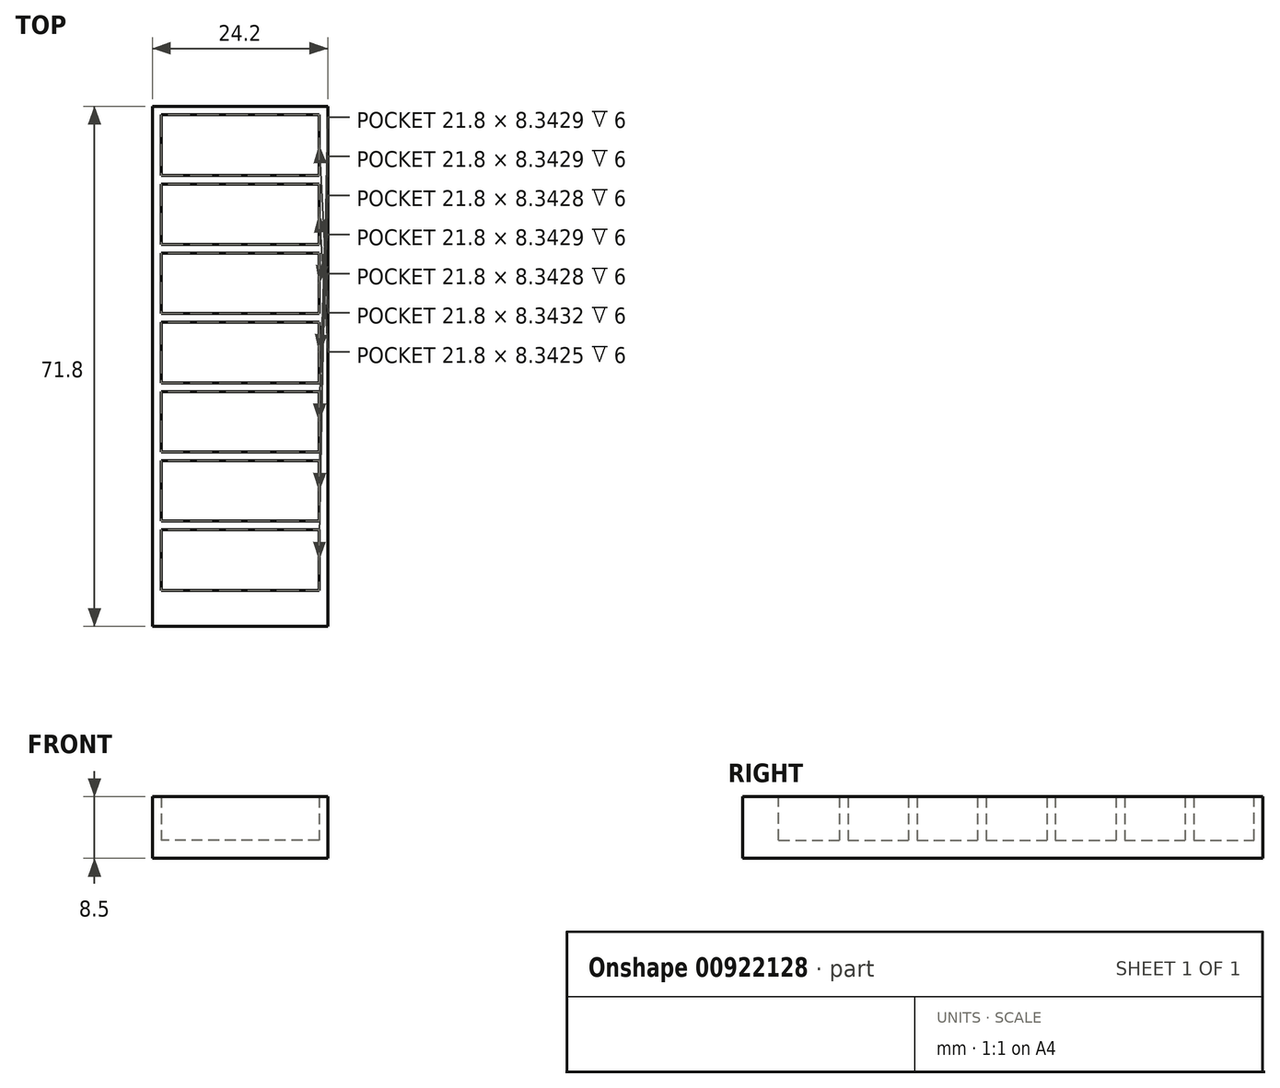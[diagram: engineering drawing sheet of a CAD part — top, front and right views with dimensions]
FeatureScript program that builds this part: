
annotation { "Feature Type Name" : "Feature", "Feature Type Description" : "" }
export const myFeature = defineFeature(function(context is Context, id is Id, definition is map)
    precondition{}
    {
        {
            var Q0;
            Q0=qCreatedBy(makeId("Top.planeOp"),FACE);
            var sketch = newSketch(context, id + "F0", { "sketchPlane" : qUnion([Q0])});
            skLineSegment(sketch, "E0.bottom", {"start": v(0, 0) * mm, "end": v(24.2, 0) * mm});
            skLineSegment(sketch, "E0.top", {"start": v(0, 71.8) * mm, "end": v(24.2, 71.8) * mm});
            skLineSegment(sketch, "E0.left", {"start": v(0, 0) * mm, "end": v(0, 71.8) * mm});
            skLineSegment(sketch, "E0.right", {"start": v(24.2, 0) * mm, "end": v(24.2, 71.8) * mm});
            skSolve(sketch);
        }
        {
            var Q0;
            Q0=qSketchRegion(id+"F0",true);
            extrude(context, id + "F1", {"entities" : qUnion([Q0]), "depth" : 8.5 * mm, "offsetDistance" : 25 * mm});
        }
        {
            var Q0;
            Q0=makeQuery(id+"F1.opExtrude","CAP_FACE",FACE,{"disambiguationData":[OSD([sQuery(id+"F0.wireOp",EDGE,"E0.bottom"),sQuery(id+"F0.wireOp",EDGE,"E0.top"),sQuery(id+"F0.wireOp",EDGE,"E0.left"),sQuery(id+"F0.wireOp",EDGE,"E0.right")])],"isStart":false});
            var sketch = newSketch(context, id + "F2", { "sketchPlane" : qUnion([Q0])});
            skLineSegment(sketch, "E1.0", {"start": v(1.2, 70.6) * mm, "end": v(23, 70.6) * mm});
            skLineSegment(sketch, "E2.0", {"start": v(23, 5) * mm, "end": v(23, 70.6) * mm});
            skLineSegment(sketch, "E3.0", {"start": v(1.2, 5) * mm, "end": v(1.2, 70.6) * mm});
            skLineSegment(sketch, "E4.0", {"start": v(1.2, 5) * mm, "end": v(23, 5) * mm});
            skSolve(sketch);
        }
        {
            var Q0;
            Q0=qSketchRegion(id+"F2",true);
            extrude(context, id + "F3", {"entities" : qUnion([Q0]), "operationType" : NewBodyOperationType.REMOVE, "oppositeDirection" : true, "depth" : 6 * mm, "offsetDistance" : 25 * mm});
        }
        {
            var Q0;
            Q0=makeQuery(id+"F3.boolean.opBoolean","COPY",FACE,{"derivedFrom":makeQuery(id+"F3.opExtrude","CAP_FACE",FACE,{"disambiguationData":[OSD([sQuery(id+"F2.wireOp",EDGE,"E1.0"),sQuery(id+"F2.wireOp",EDGE,"E2.0"),sQuery(id+"F2.wireOp",EDGE,"E3.0"),sQuery(id+"F2.wireOp",EDGE,"E4.0")])],"isStart":false})});
            var sketch = newSketch(context, id + "F4", { "sketchPlane" : qUnion([Q0])});
            skLineSegment(sketch, "E5.bottom", {"start": v(12, 70.6) * mm, "end": v(13.2, 70.6) * mm});
            skLineSegment(sketch, "E5.top", {"start": v(12, 5) * mm, "end": v(13.2, 5) * mm});
            skLineSegment(sketch, "E6.bottom", {"start": v(11, 70.6) * mm, "end": v(12.2, 70.6) * mm});
            skLineSegment(sketch, "E6.top", {"start": v(11, 5) * mm, "end": v(12.2, 5) * mm});
            skLineSegment(sketch, "E7", {"start": v(23, 70.6) * mm, "end": v(23, 5) * mm, "construction": true});
            skLineSegment(sketch, "E8", {"start": v(23, 5) * mm, "end": v(1.2, 5) * mm, "construction": true});
            skLineSegment(sketch, "E9.bottom", {"start": v(1.2, 62.26) * mm, "end": v(12.18, 62.26) * mm});
            skLineSegment(sketch, "E9.top", {"start": v(1.2, 61.06) * mm, "end": v(12, 61.06) * mm});
            skLineSegment(sketch, "E9.left", {"start": v(1.2, 62.26) * mm, "end": v(1.2, 61.06) * mm});
            skLineSegment(sketch, "E9.right", {"start": v(23, 62.26) * mm, "end": v(23, 61.06) * mm});
            skLineSegment(sketch, "E10.bottom", {"start": v(23, 52.71) * mm, "end": v(12.2, 52.71) * mm});
            skLineSegment(sketch, "E10.top", {"start": v(23, 51.51) * mm, "end": v(12.2, 51.51) * mm});
            skLineSegment(sketch, "E10.left", {"start": v(23, 52.71) * mm, "end": v(23, 51.51) * mm});
            skLineSegment(sketch, "E10.right", {"start": v(1.2, 52.71) * mm, "end": v(1.2, 51.51) * mm});
            skLineSegment(sketch, "E11.bottom", {"start": v(1.2, 43.17) * mm, "end": v(12, 43.17) * mm});
            skLineSegment(sketch, "E11.top", {"start": v(1.2, 41.97) * mm, "end": v(12, 41.97) * mm});
            skLineSegment(sketch, "E11.left", {"start": v(1.2, 43.17) * mm, "end": v(1.2, 41.97) * mm});
            skLineSegment(sketch, "E11.right", {"start": v(23, 43.17) * mm, "end": v(23, 41.97) * mm});
            skLineSegment(sketch, "E12.bottom", {"start": v(23, 33.63) * mm, "end": v(12.2, 33.63) * mm});
            skLineSegment(sketch, "E12.top", {"start": v(23, 32.43) * mm, "end": v(12.2, 32.43) * mm});
            skLineSegment(sketch, "E12.left", {"start": v(23, 33.63) * mm, "end": v(23, 32.43) * mm});
            skLineSegment(sketch, "E12.right", {"start": v(1.2, 33.63) * mm, "end": v(1.2, 32.43) * mm});
            skLineSegment(sketch, "E13.bottom", {"start": v(1.2, 24.09) * mm, "end": v(12, 24.09) * mm});
            skLineSegment(sketch, "E13.top", {"start": v(1.2, 22.89) * mm, "end": v(12, 22.89) * mm});
            skLineSegment(sketch, "E13.left", {"start": v(1.2, 24.09) * mm, "end": v(1.2, 22.89) * mm});
            skLineSegment(sketch, "E13.right", {"start": v(23, 24.09) * mm, "end": v(23, 22.89) * mm});
            skLineSegment(sketch, "E14.bottom", {"start": v(23, 14.54) * mm, "end": v(12.2, 14.54) * mm});
            skLineSegment(sketch, "E14.top", {"start": v(23, 13.34) * mm, "end": v(12.2, 13.34) * mm});
            skLineSegment(sketch, "E14.left", {"start": v(23, 14.54) * mm, "end": v(23, 13.34) * mm});
            skLineSegment(sketch, "E14.right", {"start": v(1.2, 14.54) * mm, "end": v(1.2, 13.34) * mm});
            skLineSegment(sketch, "E15.trimOffspring", {"start": v(1, 62.26) * mm, "end": v(11, 62.26) * mm});
            skLineSegment(sketch, "E16.trimOffspring", {"start": v(11, 61.06) * mm, "end": v(13.2, 61.06) * mm});
            skLineSegment(sketch, "E17.trimOffspring", {"start": v(12.02, 62.26) * mm, "end": v(23, 62.26) * mm});
            skLineSegment(sketch, "E18.trimOffspring", {"start": v(12.2, 61.06) * mm, "end": v(23, 61.06) * mm});
            skLineSegment(sketch, "E19.trimOffspring", {"start": v(13.2, 52.71) * mm, "end": v(11, 52.71) * mm});
            skLineSegment(sketch, "E20.trimOffspring", {"start": v(13.2, 51.51) * mm, "end": v(11, 51.51) * mm});
            skLineSegment(sketch, "E21.trimOffspring", {"start": v(12, 52.71) * mm, "end": v(1.2, 52.71) * mm});
            skLineSegment(sketch, "E22.trimOffspring", {"start": v(12, 51.51) * mm, "end": v(1.2, 51.51) * mm});
            skLineSegment(sketch, "E23.trimOffspring", {"start": v(11, 43.17) * mm, "end": v(13.2, 43.17) * mm});
            skLineSegment(sketch, "E24.trimOffspring", {"start": v(11, 41.97) * mm, "end": v(13.2, 41.97) * mm});
            skLineSegment(sketch, "E25.trimOffspring", {"start": v(12.2, 43.17) * mm, "end": v(23, 43.17) * mm});
            skLineSegment(sketch, "E26.trimOffspring", {"start": v(12.2, 41.97) * mm, "end": v(23, 41.97) * mm});
            skLineSegment(sketch, "E27.trimOffspring", {"start": v(13.2, 33.63) * mm, "end": v(11, 33.63) * mm});
            skLineSegment(sketch, "E28.trimOffspring", {"start": v(13.2, 32.43) * mm, "end": v(11, 32.43) * mm});
            skLineSegment(sketch, "E29.trimOffspring", {"start": v(12, 33.63) * mm, "end": v(1.2, 33.63) * mm});
            skLineSegment(sketch, "E30.trimOffspring", {"start": v(12, 32.43) * mm, "end": v(1.2, 32.43) * mm});
            skLineSegment(sketch, "E31.trimOffspring", {"start": v(11, 24.09) * mm, "end": v(13.2, 24.09) * mm});
            skLineSegment(sketch, "E32.trimOffspring", {"start": v(11, 22.89) * mm, "end": v(13.2, 22.89) * mm});
            skLineSegment(sketch, "E33.trimOffspring", {"start": v(12.2, 24.09) * mm, "end": v(23, 24.09) * mm});
            skLineSegment(sketch, "E34.trimOffspring", {"start": v(12.2, 22.89) * mm, "end": v(23, 22.89) * mm});
            skLineSegment(sketch, "E35.trimOffspring", {"start": v(13.2, 14.54) * mm, "end": v(11, 14.54) * mm});
            skLineSegment(sketch, "E36.trimOffspring", {"start": v(13.2, 13.34) * mm, "end": v(11, 13.34) * mm});
            skLineSegment(sketch, "E37.trimOffspring", {"start": v(12, 14.54) * mm, "end": v(1.2, 14.54) * mm});
            skLineSegment(sketch, "E38.trimOffspring", {"start": v(12, 13.34) * mm, "end": v(1.2, 13.34) * mm});
            skLineSegment(sketch, "E39", {"start": v(1, 62.26) * mm, "end": v(12.18, 62.26) * mm});
            skLineSegment(sketch, "E40", {"start": v(13.2, 61.06) * mm, "end": v(12, 61.06) * mm});
            skLineSegment(sketch, "E41", {"start": v(12, 52.71) * mm, "end": v(13.2, 52.71) * mm});
            skLineSegment(sketch, "E42", {"start": v(13.2, 51.51) * mm, "end": v(12, 51.51) * mm});
            skLineSegment(sketch, "E43", {"start": v(12, 43.17) * mm, "end": v(13.2, 43.17) * mm});
            skLineSegment(sketch, "E44", {"start": v(13.2, 41.97) * mm, "end": v(12, 41.97) * mm});
            skLineSegment(sketch, "E45", {"start": v(12, 33.63) * mm, "end": v(13.2, 33.63) * mm});
            skLineSegment(sketch, "E46", {"start": v(13.2, 32.43) * mm, "end": v(12, 32.43) * mm});
            skLineSegment(sketch, "E47", {"start": v(12, 24.09) * mm, "end": v(13.2, 24.09) * mm});
            skLineSegment(sketch, "E48", {"start": v(13.2, 22.89) * mm, "end": v(12, 22.89) * mm});
            skLineSegment(sketch, "E49", {"start": v(12, 14.54) * mm, "end": v(13.2, 14.54) * mm});
            skLineSegment(sketch, "E50", {"start": v(13.2, 13.34) * mm, "end": v(12, 13.34) * mm});
            skSolve(sketch);
        }
        {
            var Q0;
            Q0=qSketchRegion(id+"F4",true);
            extrude(context, id + "F5", {"entities" : qUnion([Q0]), "operationType" : NewBodyOperationType.ADD, "depth" : 6 * mm, "offsetDistance" : 25 * mm});
        }
        {
            var Q0;
            Q0=makeQuery(id+"F1.opExtrude","SWEPT_BODY",BODY,{"disambiguationData":[OSD([sQuery(id+"F0.wireOp",EDGE,"E0.bottom"),sQuery(id+"F0.wireOp",EDGE,"E0.top"),sQuery(id+"F0.wireOp",EDGE,"E0.left"),sQuery(id+"F0.wireOp",EDGE,"E0.right")])]});
            transform(context, id + "F6", {"entities" : qUnion([Q0]), "transformType" : TransformType.TRANSLATION_3D, "dx" : 0 * mm, "dy" : 0 * mm, "dz" : 0 * mm, "makeCopy" : true});
        }
        {
            var Q0;
            Q0=makeQuery(id+"F6.opPattern","COPY",BODY,{"derivedFrom":makeQuery(id+"F1.opExtrude","SWEPT_BODY",BODY,{"disambiguationData":[OSD([sQuery(id+"F0.wireOp",EDGE,"E0.bottom"),sQuery(id+"F0.wireOp",EDGE,"E0.top"),sQuery(id+"F0.wireOp",EDGE,"E0.left"),sQuery(id+"F0.wireOp",EDGE,"E0.right")])]}),"instanceName":"1"});
            deleteBodies(context, id + "F7", {"entities" : qUnion([Q0])});
        }
    });
